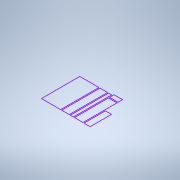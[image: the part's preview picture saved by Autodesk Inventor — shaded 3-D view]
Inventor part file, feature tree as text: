
AUTODESK INVENTOR PART (.ipt)
format: ipt  version: 2022 (Build 260153000, 153)  size: 115,200 bytes
history: native  units: mm
features: sketch x2, other x1, extrude x1
ambient origin geometry x8: Origin, YZ Plane, XZ Plane, XY Plane, X Axis, Y Axis, Z Axis, Center Point
bodies: Body1 (feature_tree)
feature tree (4):
  other  "ソリッド1"
  extrude  "押し出し1"  Depth=500.0mm
  sketch  "スケッチ2"
  sketch  "スケッチ1"
